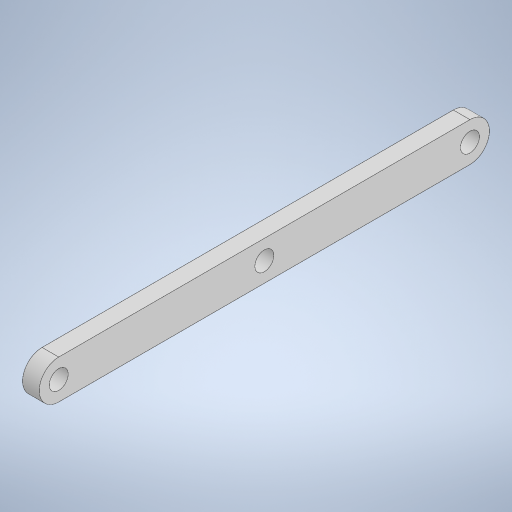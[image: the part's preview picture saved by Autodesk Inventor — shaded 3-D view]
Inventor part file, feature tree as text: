
AUTODESK INVENTOR PART (.ipt)
format: ipt  version: 2024.3 (Build 283343000, 343)  size: 264,192 bytes
history: native  units: mm
features: sketch x3, extrude x3, hole x1, split x1, projected_geometry x1
ambient origin geometry x8: Origin, YZ Plane, XZ Plane, XY Plane, X Axis, Y Axis, Z Axis, Center Point
bodies: Body1 (feature_tree)
feature tree (9):
  sketch  "Sketch1"  dims[d14=7.0mm d15=81.0mm]
  extrude  "Extrusión3"  Depth=7.0mm
  extrude  "Extrusión4"  Depth=3.0mm TaperAngle=0.0deg
  hole  "Agujero1"  [1 undecoded]
  split  "Dividir1"
  extrude  "Extrusión5"  [1 undecoded]
  sketch  "Boceto2"  dims[d16=3.0mm d17=16.0mm d18=0.0mm]
  sketch  "Boceto3"  dims[d19=10.0mm d20=0.0mm d21=3.4mm d22=6.0mm d23=6.3mm d24=2.0mm d25=90.0deg d26=8.0mm d27=20.594885mm d28=10.0mm d29=0.0mm]
  projected_geometry  "Contorno proyectado1"
note: 2 required parameter values undecoded (feature->parameter linkage not recoverable at this tier; creation-order binding heuristic only, values carry confidence <= 0.55)
